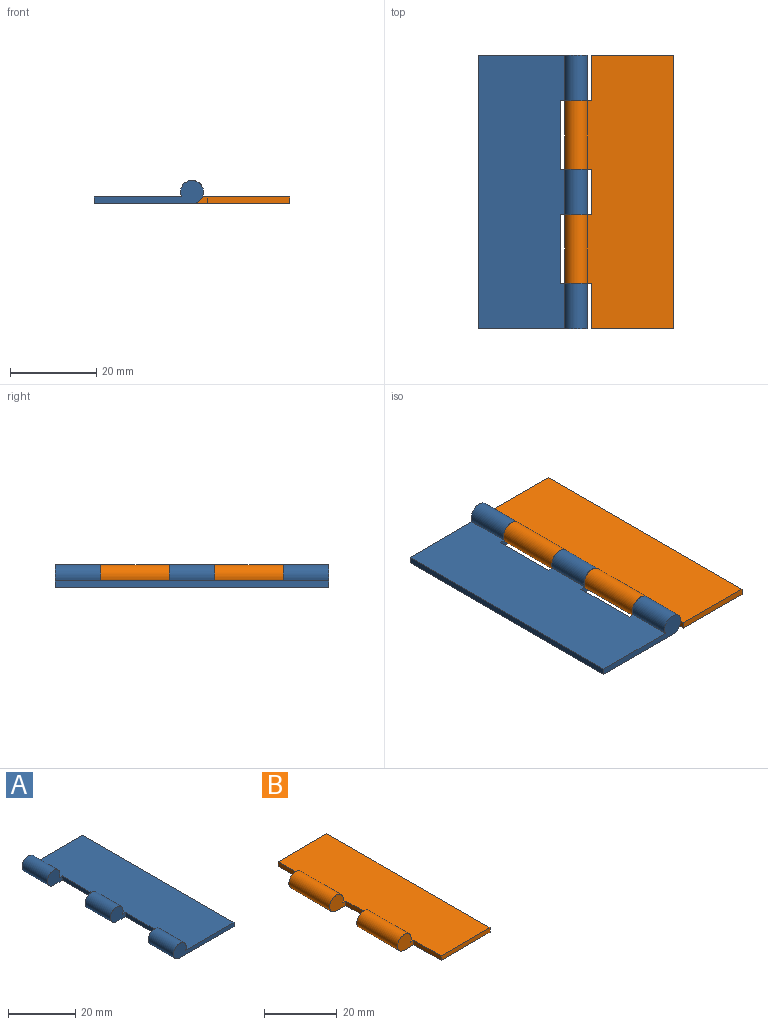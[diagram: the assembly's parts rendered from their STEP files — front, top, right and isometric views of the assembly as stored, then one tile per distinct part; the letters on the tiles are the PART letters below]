
ASSEMBLY  parts=2 mates=1
PART A: 14 faces, bbox 25.4x63.5x5.3 mm
  f0: cylinder r=2.67mm len=10.58mm, axis (0,1,0), area 145.5mm2, adj f3,f5,f8,f12
  f1: cylinder r=2.67mm len=10.58mm, axis (0,1,0), area 145.5mm2, adj f3,f5,f6,f9
  f2: cylinder r=2.67mm len=10.58mm, axis (0,1,0), area 145.5mm2, adj f3,f5,f7,f11
  f3: plane 63.5x22.73mm, normal (0,0,-1), area 1326.6mm2, adj f0,f1,f2,f4,f6,f7,f8,f9
  f4: plane 63.5x1.52mm, normal (1,0,0), area 96.8mm2, adj f3,f5,f6,f7
  f5: plane 63.5x20.32mm, normal (0,0,1), area 1250.1mm2, adj f0,f1,f2,f4,f6,f7,f8,f9
  f6: plane 25.4x5.33mm, normal (0,-1,0), area 54.4mm2, adj f1,f3,f4,f5
  f7: plane 25.4x5.33mm, normal (0,1,0), area 54.4mm2, adj f2,f3,f4,f5
  f8: plane 6.35x5.33mm, normal (0,-1,0), area 25.3mm2, adj f0,f3,f5,f10
  f9: plane 6.35x5.33mm, normal (0,1,0), area 25.3mm2, adj f1,f3,f5,f10
  f10: plane 15.88x1.52mm, normal (-1,0,0), area 24.2mm2, adj f3,f5,f8,f9
  f11: plane 6.35x5.33mm, normal (0,-1,0), area 25.3mm2, adj f2,f3,f5,f13
  f12: plane 6.35x5.33mm, normal (0,1,0), area 25.3mm2, adj f0,f3,f5,f13
  f13: plane 15.88x1.52mm, normal (-1,0,0), area 24.2mm2, adj f3,f5,f11,f12
PART B: 14 faces, bbox 25.4x63.5x5.3 mm
  f0: cylinder r=2.67mm len=15.88mm, axis (0,-1,0), area 218.3mm2, adj f2,f3,f9,f12
  f1: cylinder r=2.67mm len=15.88mm, axis (0,-1,0), area 218.3mm2, adj f2,f3,f7,f10
  f2: plane 63.5x22.73mm, normal (0,0,-1), area 1326.6mm2, adj f0,f1,f4,f5,f6,f7,f8,f9
  f3: plane 63.5x20.32mm, normal (0,0,1), area 1250.1mm2, adj f0,f1,f4,f5,f6,f7,f8,f9
  f4: plane 19.05x1.52mm, normal (0,1,0), area 29mm2, adj f2,f3,f6,f13
  f5: plane 19.05x1.52mm, normal (0,-1,0), area 29mm2, adj f2,f3,f6,f8
  f6: plane 63.5x1.52mm, normal (1,0,0), area 96.8mm2, adj f2,f3,f4,f5
  f7: plane 6.35x5.33mm, normal (0,-1,0), area 25.3mm2, adj f1,f2,f3,f8
  f8: plane 10.58x1.52mm, normal (-1,0,0), area 16.1mm2, adj f2,f3,f5,f7
  f9: plane 6.35x5.33mm, normal (0,-1,0), area 25.3mm2, adj f0,f2,f3,f11
  f10: plane 6.35x5.33mm, normal (0,1,0), area 25.3mm2, adj f1,f2,f3,f11
  f11: plane 10.58x1.52mm, normal (-1,0,0), area 16.1mm2, adj f2,f3,f9,f10
  f12: plane 6.35x5.33mm, normal (0,1,0), area 25.3mm2, adj f0,f2,f3,f13
  f13: plane 10.58x1.52mm, normal (-1,0,0), area 16.1mm2, adj f2,f3,f4,f12
PLACE A rot(axis=(0,0,1),180deg) t=(-34.94,-31.75,0)mm
PLACE B t=(10.53,-31.75,0)mm
MATE revolute B.f0 <-> A.f0  axis (0,-1,0) through (-12.21,-21.17,2.67)mm
